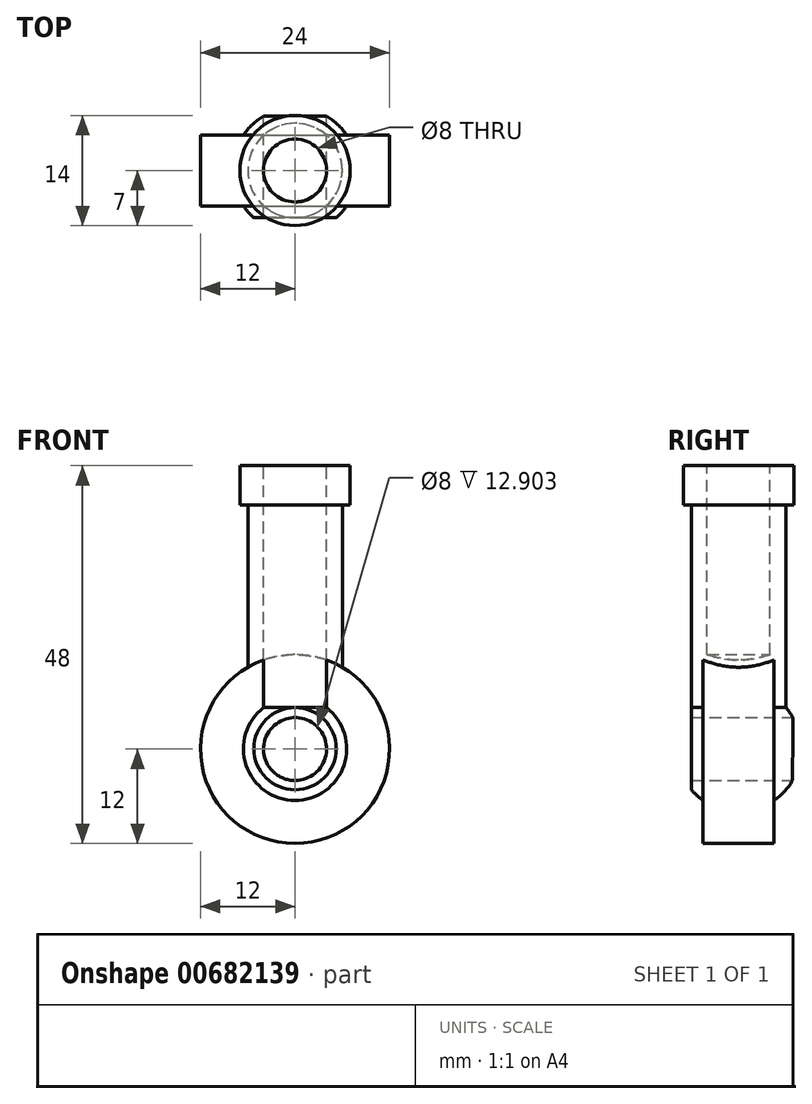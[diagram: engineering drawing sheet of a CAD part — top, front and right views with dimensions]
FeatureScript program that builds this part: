
annotation { "Feature Type Name" : "Feature", "Feature Type Description" : "" }
export const myFeature = defineFeature(function(context is Context, id is Id, definition is map)
    precondition{}
    {
        {
            var Q0;
            Q0=qCreatedBy(makeId("Front.planeOp"),FACE);
            var sketch = newSketch(context, id + "F0", { "sketchPlane" : qUnion([Q0])});
            skLineSegment(sketch, "E0", {"start": v(0, 8) * mm, "end": v(0, -8) * mm});
            skArc(sketch, "E1", {"start": v(-0.24, -7.91) * mm, "mid": v(7.96, -0.08) * mm, "end": v(0, 8) * mm});
            skSolve(sketch);
        }
        {
            var Q0;
            {var subQ0=sQuery(id+"F0.wireOp",EDGE,"E1");var subQ1=sQuery(id+"F0.wireOp",EDGE,"E0");var subQ2=makeQuery(id+"F0.imprint","INTERSECT",VERTEX,{"disambiguationData":[OD(0.0)],"derivedFrom":[subQ1,subQ0]});Q0=makeQuery(id+"F0.imprint","IMPRINT",FACE,{"disambiguationData":[TD([[makeQuery(id+"F0.imprint","IMPRINT",EDGE,{"disambiguationData":[TD([[subQ2,-1.0]])],"derivedFrom":subQ1}),1.0]])]});}
            var Q1;
            Q1=sQuery(id+"F0.wireOp",EDGE,"E0");
            revolve(context, id + "F1", {"entities" : qUnion([Q0]), "axis" : qUnion([Q1]), "revolveType" : RevolveType.FULL});
        }
        {
            var Q0;
            Q0=qCreatedBy(makeId("Front.planeOp"),FACE);
            var sketch = newSketch(context, id + "F2", { "sketchPlane" : qUnion([Q0])});
            skCircle(sketch, "E2", {"center": v(0, 0) * mm, "radius": 4 * mm});
            skSolve(sketch);
        }
        {
            var Q0;
            Q0 = qSketchRegion(id + "F2", true);
            extrude(context, id + "F3", {"entities" : qUnion([Q0]), "operationType" : NewBodyOperationType.REMOVE, "endBound" : BoundingType.SYMMETRIC, "depth" : 25 * mm, "offsetDistance" : 25 * mm});
        }
        {
            var Q0;
            Q0=qCreatedBy(makeId("Front.planeOp"),FACE);
            cPlane(context, id + "F4", {"entities" : qUnion([Q0]), "cplaneType" : CPlaneType.OFFSET, "offset" : 6 * mm, "width" : 150 * mm, "height" : 150 * mm});
        }
        {
            var Q0;
            Q0=qCreatedBy(id+"F4.planeOp",FACE);
            var sketch = newSketch(context, id + "F5", { "sketchPlane" : qUnion([Q0])});
            skCircle(sketch, "E3", {"center": v(0, 0) * mm, "radius": 17.48 * mm});
            skSolve(sketch);
        }
        {
            var Q0;
            Q0 = qSketchRegion(id + "F5", true);
            extrude(context, id + "F6", {"entities" : qUnion([Q0]), "operationType" : NewBodyOperationType.REMOVE, "endBound" : BoundingType.THROUGH_ALL, "depth" : 25 * mm, "offsetDistance" : 25 * mm});
        }
        {
            var Q0;
            Q0=qCreatedBy(makeId("Front.planeOp"),FACE);
            var sketch = newSketch(context, id + "F7", { "sketchPlane" : qUnion([Q0])});
            skCircle(sketch, "E4", {"center": v(0, 0) * mm, "radius": 12 * mm});
            skCircle(sketch, "E5", {"center": v(0, 0) * mm, "radius": 4.06 * mm});
            skSolve(sketch);
        }
        {
            var Q0;
            Q0 = qSketchRegion(id + "F7", true);
            extrude(context, id + "F8", {"entities" : qUnion([Q0]), "operationType" : NewBodyOperationType.ADD, "endBound" : BoundingType.SYMMETRIC, "depth" : 9 * mm, "offsetDistance" : 25 * mm});
        }
        {
            var Q0;
            Q0=qCreatedBy(makeId("Top.planeOp"),FACE);
            cPlane(context, id + "F9", {"entities" : qUnion([Q0]), "cplaneType" : CPlaneType.OFFSET, "offset" : 36 * mm, "width" : 150 * mm, "height" : 150 * mm});
        }
        {
            var Q0;
            Q0=qCreatedBy(id+"F9.planeOp",FACE);
            var sketch = newSketch(context, id + "F10", { "sketchPlane" : qUnion([Q0])});
            skCircle(sketch, "E6", {"center": v(0, 0) * mm, "radius": 4 * mm});
            skCircle(sketch, "E7", {"center": v(0, 0) * mm, "radius": 6 * mm});
            skSolve(sketch);
        }
        {
            var Q0;
            Q0=makeQuery(id+"F10.imprint","IMPRINT",FACE,{"disambiguationData":[TD([[makeQuery(id+"F10.imprint","IMPRINT",EDGE,{"derivedFrom":sQuery(id+"F10.wireOp",EDGE,"E6")}),-1.0]])]});
            extrude(context, id + "F11", {"entities" : qUnion([Q0]), "operationType" : NewBodyOperationType.ADD, "endBound" : BoundingType.UP_TO_NEXT, "oppositeDirection" : true, "depth" : 25 * mm, "offsetDistance" : 25 * mm});
        }
        {
            var Q0;
            Q0=makeQuery(id+"F11.opExtrude","CAP_FACE",FACE,{"disambiguationData":[OSD([sQuery(id+"F10.wireOp",EDGE,"E6"),sQuery(id+"F10.wireOp",EDGE,"E7")])],"isStart":true});
            var sketch = newSketch(context, id + "F12", { "sketchPlane" : qUnion([Q0])});
            skCircle(sketch, "E8", {"center": v(0, 0) * mm, "radius": 6 * mm});
            skCircle(sketch, "E9", {"center": v(0, 0) * mm, "radius": 7 * mm});
            skSolve(sketch);
        }
        {
            var Q0;
            Q0 = qSketchRegion(id + "F12", true);
            extrude(context, id + "F13", {"entities" : qUnion([Q0]), "operationType" : NewBodyOperationType.ADD, "oppositeDirection" : true, "depth" : 5 * mm, "offsetDistance" : 25 * mm});
        }
    });
